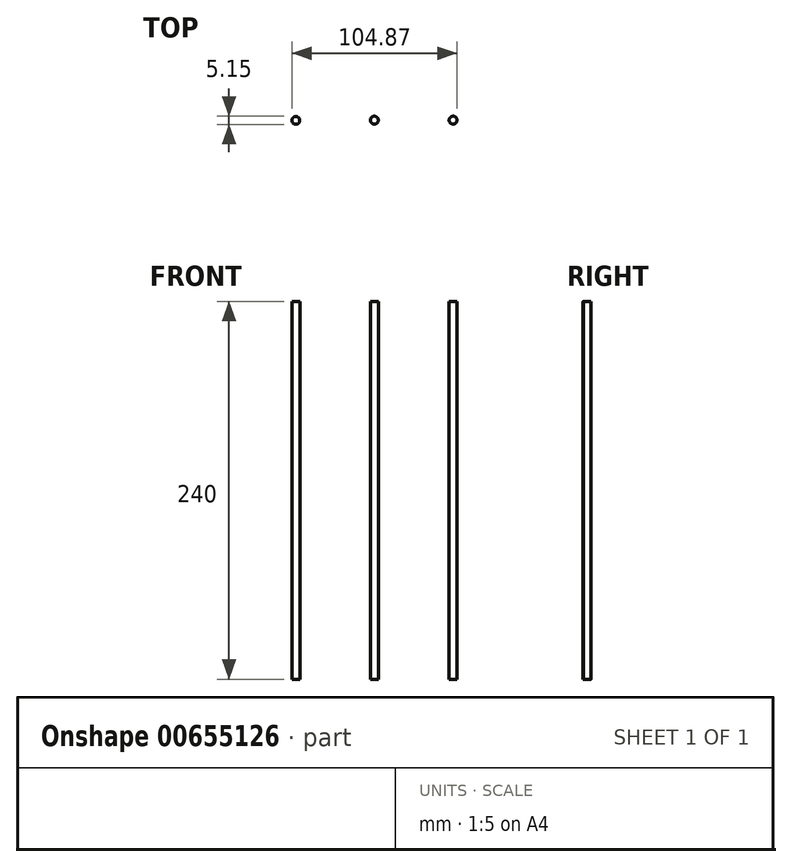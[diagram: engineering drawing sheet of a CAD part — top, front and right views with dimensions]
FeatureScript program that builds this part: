
annotation { "Feature Type Name" : "Feature", "Feature Type Description" : "" }
export const myFeature = defineFeature(function(context is Context, id is Id, definition is map)
    precondition{}
    {
        {
            var Q0;
            Q0=qCreatedBy(makeId("Top.planeOp"),FACE);
            var sketch = newSketch(context, id + "F0", { "sketchPlane" : qUnion([Q0])});
            skCircle(sketch, "E0", {"center": v(0, 0) * mm, "radius": 2.5 * mm});
            skCircle(sketch, "E1", {"center": v(50, 0) * mm, "radius": 2.5 * mm});
            skLineSegment(sketch, "E2", {"start": v(0, 42.15) * mm, "end": v(0.12, -36.42) * mm, "construction": true});
            skCircle(sketch, "E3", {"center": v(-49.87, -0.15) * mm, "radius": 2.5 * mm});
            skSolve(sketch);
        }
        {
            var Q0;
            Q0 = qSketchRegion(id + "F0", true);
            extrude(context, id + "F1", {"entities" : qUnion([Q0]), "depth" : 220 * mm, "offsetDistance" : 25.4 * mm, "hasSecondDirection" : true, "secondDirectionOppositeDirection" : true, "secondDirectionDepth" : 20 * mm});
        }
    });
